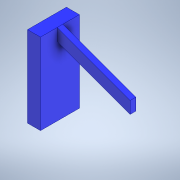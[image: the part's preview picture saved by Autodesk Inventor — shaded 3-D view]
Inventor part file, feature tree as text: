
AUTODESK INVENTOR PART (.ipt)
format: ipt  version: 2022.2 (Build 262287000, 287)  size: 111,104 bytes
history: native  units: in
note: dims shown in document units (in); Inventor stores cm internally (conversion verified against a paired STEP export)
features: extrude x2, sketch x1
ambient origin geometry x8: Origin, YZ Plane, XZ Plane, XY Plane, X Axis, Y Axis, Z Axis, Center Point
bodies: Solid1 (feature_tree)
feature tree (3):
  sketch  "Sketch1"  dims[d0=25.0in d1=24.0in d2=0.1374in d3=3.5in d4=4.0in d5=12.0in d6=0.0in d7=1.75in d8=0.0in]
  extrude  "Extrusion1"  Depth=24.0in
  extrude  "Extrusion2"  Depth=1.75in
